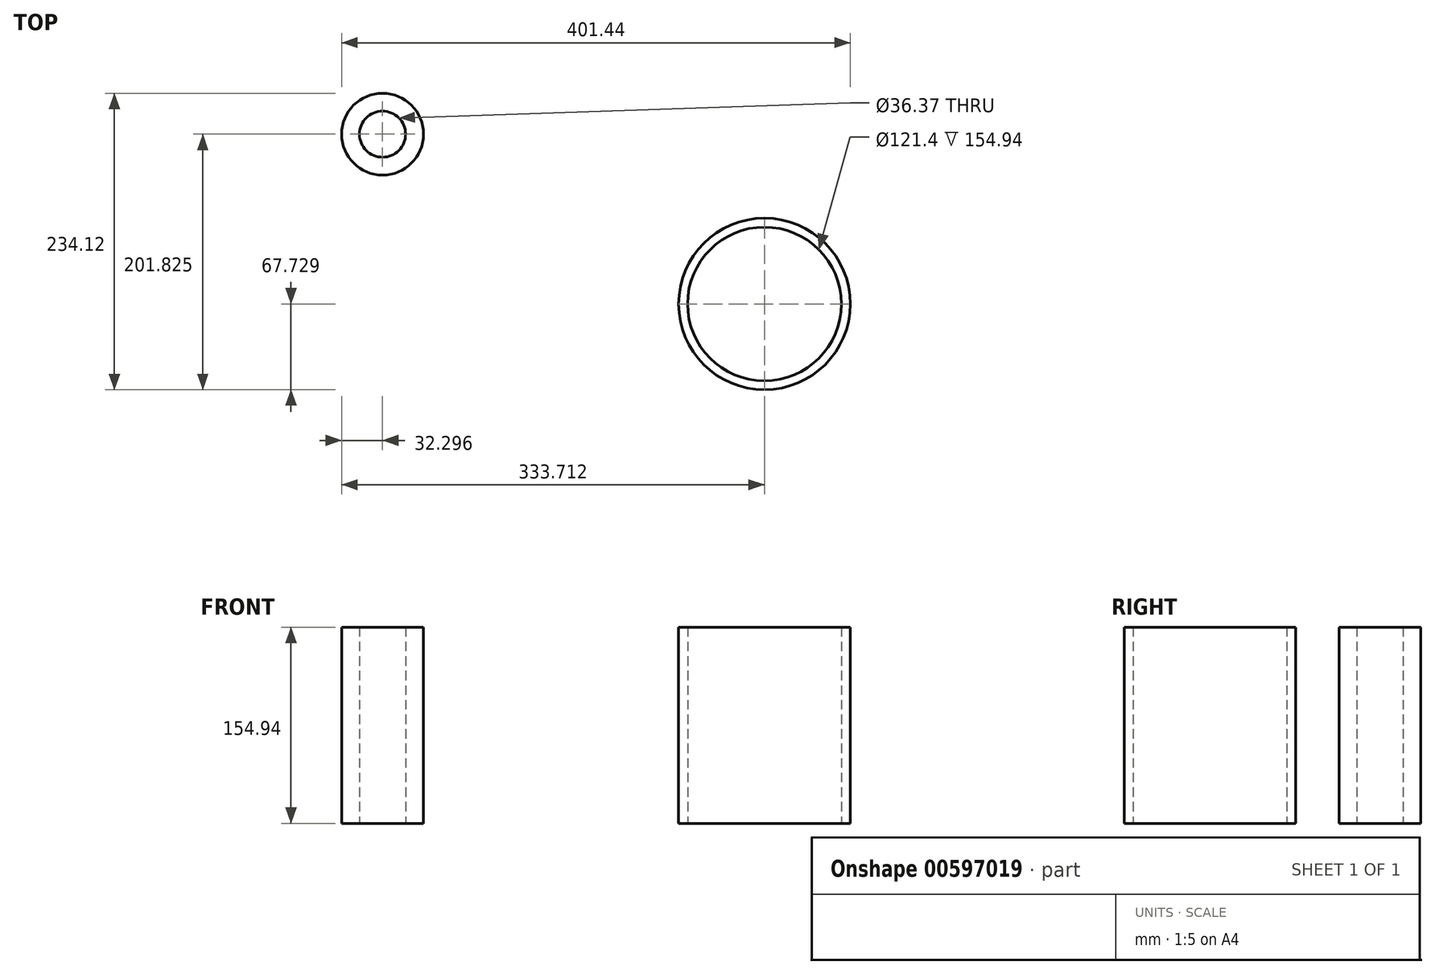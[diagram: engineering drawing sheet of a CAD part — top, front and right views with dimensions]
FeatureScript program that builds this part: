
annotation { "Feature Type Name" : "Feature", "Feature Type Description" : "" }
export const myFeature = defineFeature(function(context is Context, id is Id, definition is map)
    precondition{}
    {
        {
            var Q0;
            Q0=qCreatedBy(makeId("Top.planeOp"),FACE);
            var sketch = newSketch(context, id + "F0", { "sketchPlane" : qUnion([Q0])});
            skCircle(sketch, "E0", {"center": v(-447.91, 169.44) * mm, "radius": 18.19 * mm});
            skCircle(sketch, "E1", {"center": v(-447.91, 169.44) * mm, "radius": 32.3 * mm});
            skCircle(sketch, "E2", {"center": v(-146.5, 35.35) * mm, "radius": 67.73 * mm});
            skCircle(sketch, "E3", {"center": v(-146.5, 35.35) * mm, "radius": 60.7 * mm});
            skSolve(sketch);
        }
        {
            var Q0;
            Q0 = qSketchRegion(id + "F0", true);
            extrude(context, id + "F1", {"entities" : qUnion([Q0]), "depth" : 154.94 * mm, "offsetDistance" : 25.4 * mm});
        }
    });
